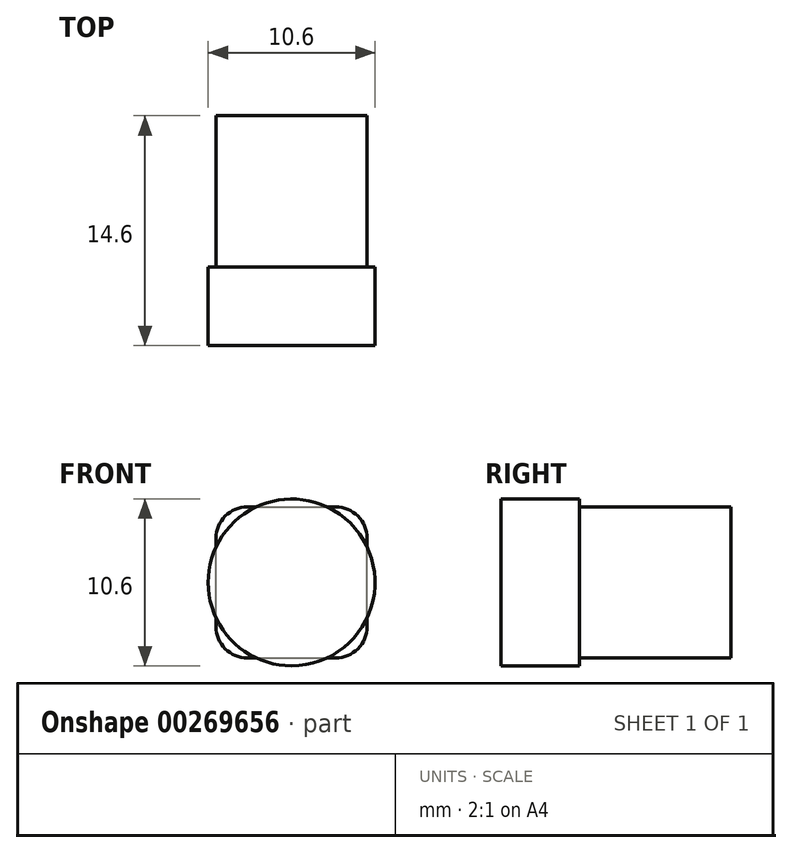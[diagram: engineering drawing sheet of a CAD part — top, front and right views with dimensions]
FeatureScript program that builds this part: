
annotation { "Feature Type Name" : "Feature", "Feature Type Description" : "" }
export const myFeature = defineFeature(function(context is Context, id is Id, definition is map)
    precondition{}
    {
        {
            var Q0;
            Q0=qCreatedBy(makeId("Front.planeOp"),FACE);
            var sketch = newSketch(context, id + "F0", { "sketchPlane" : qUnion([Q0])});
            skLineSegment(sketch, "E0.bottom", {"start": v(-4.8, -4.8) * mm, "end": v(4.8, -4.8) * mm});
            skLineSegment(sketch, "E0.top", {"start": v(-4.8, 4.8) * mm, "end": v(4.8, 4.8) * mm});
            skLineSegment(sketch, "E0.left", {"start": v(-4.8, -4.8) * mm, "end": v(-4.8, 4.8) * mm});
            skLineSegment(sketch, "E0.right", {"start": v(4.8, -4.8) * mm, "end": v(4.8, 4.8) * mm});
            skSolve(sketch);
        }
        {
            var Q0;
            Q0 = qSketchRegion(id + "F0", true);
            extrude(context, id + "F1", {"entities" : qUnion([Q0]), "oppositeDirection" : true, "depth" : 9.6 * mm});
        }
        {
            var Q0;
            Q0=qCreatedBy(makeId("Front.planeOp"),FACE);
            var sketch = newSketch(context, id + "F2", { "sketchPlane" : qUnion([Q0])});
            skCircle(sketch, "E1", {"center": v(0, 0) * mm, "radius": 5.3 * mm});
            skSolve(sketch);
        }
        {
            var Q0;
            Q0 = qSketchRegion(id + "F2", true);
            extrude(context, id + "F3", {"entities" : qUnion([Q0]), "operationType" : NewBodyOperationType.ADD, "depth" : 5 * mm});
        }
        {
            var Q0;
            Q0=makeQuery(id+"F1.opExtrude","SWEPT_EDGE",EDGE,{"disambiguationData":[OSD([sQuery(id+"F0.wireOp",EDGE,"E0.top"),sQuery(id+"F0.wireOp",EDGE,"E0.right")])]});
            var Q1;
            Q1=makeQuery(id+"F1.opExtrude","SWEPT_EDGE",EDGE,{"disambiguationData":[OSD([sQuery(id+"F0.wireOp",EDGE,"E0.top"),sQuery(id+"F0.wireOp",EDGE,"E0.left")])]});
            var Q2;
            Q2=makeQuery(id+"F1.opExtrude","SWEPT_EDGE",EDGE,{"disambiguationData":[OSD([sQuery(id+"F0.wireOp",EDGE,"E0.bottom"),sQuery(id+"F0.wireOp",EDGE,"E0.left")])]});
            var Q3;
            Q3=makeQuery(id+"F1.opExtrude","SWEPT_EDGE",EDGE,{"disambiguationData":[OSD([sQuery(id+"F0.wireOp",EDGE,"E0.bottom"),sQuery(id+"F0.wireOp",EDGE,"E0.right")])]});
            fillet(context, id + "F4", {"entities" : qUnion([Q0, Q1, Q2, Q3]), "radius" : 2 * mm, "tangentPropagation" : true, "allowEdgeOverflow" : false});
        }
    });
